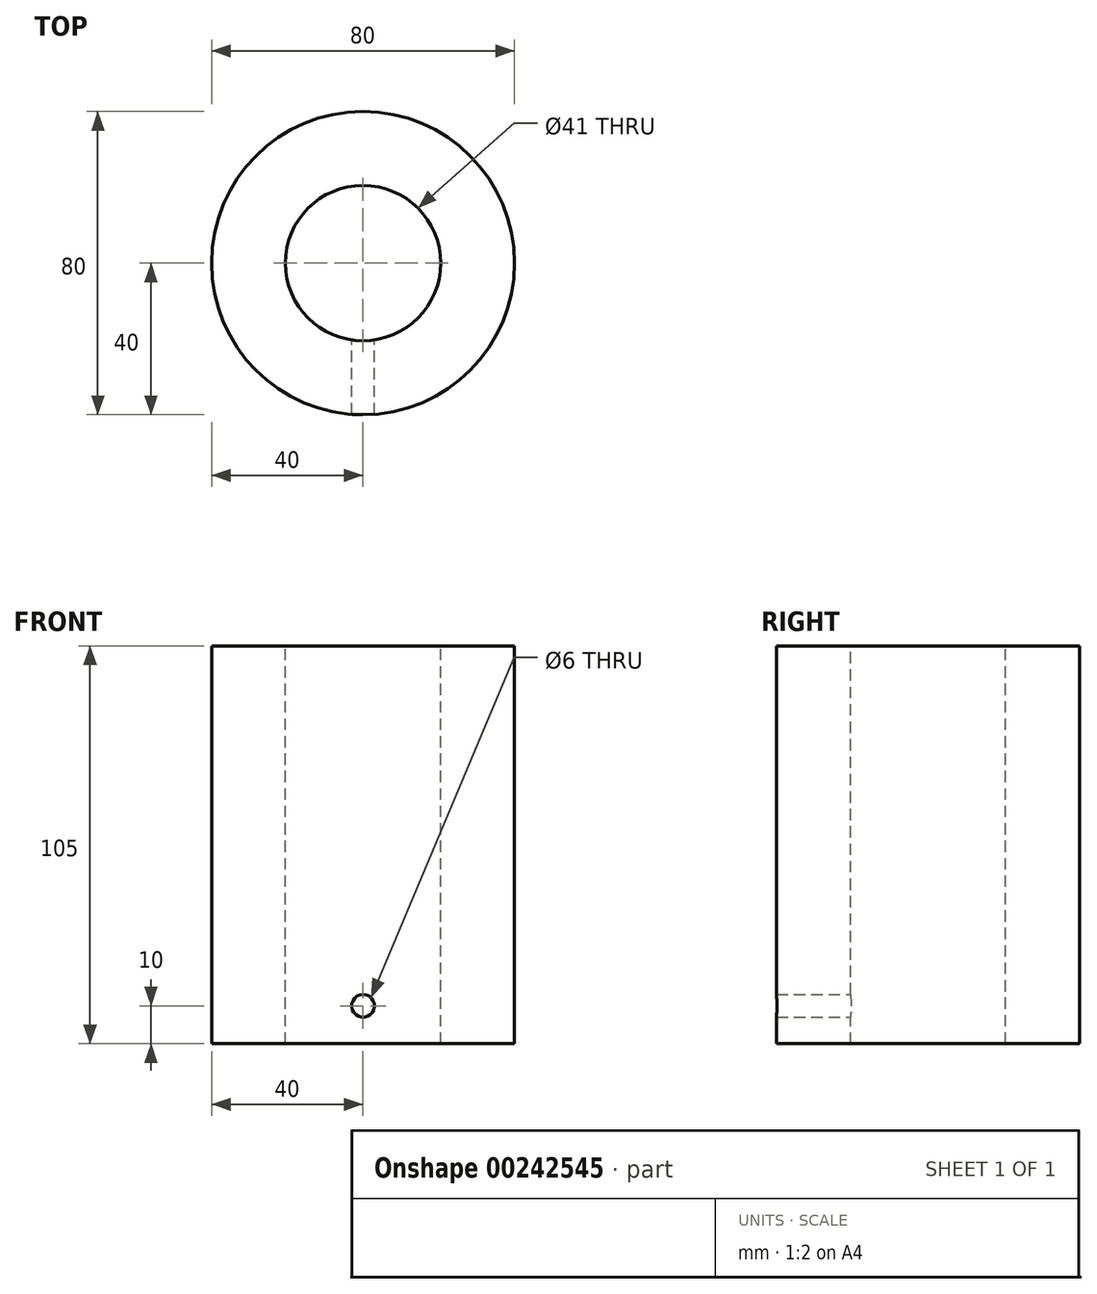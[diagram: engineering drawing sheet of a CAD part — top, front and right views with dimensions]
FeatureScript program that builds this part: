
annotation { "Feature Type Name" : "Feature", "Feature Type Description" : "" }
export const myFeature = defineFeature(function(context is Context, id is Id, definition is map)
    precondition{}
    {
        {
            var Q0;
            Q0=qCreatedBy(makeId("Top.planeOp"),FACE);
            var sketch = newSketch(context, id + "F0", { "sketchPlane" : qUnion([Q0])});
            skCircle(sketch, "E0", {"center": v(0, 0) * mm, "radius": 40 * mm});
            skSolve(sketch);
        }
        {
            var Q0;
            Q0=makeQuery(id+"F0.imprint","IMPRINT",FACE,{"disambiguationData":[TD([[makeQuery(id+"F0.imprint","IMPRINT",EDGE,{"derivedFrom":sQuery(id+"F0.wireOp",EDGE,"E0")}),1.0]])]});
            var Q1;
            Q1=sQuery(id+"F0.wireOp",EDGE,"E0");
            extrude(context, id + "F1", {"entities" : qUnion([Q0]), "surfaceEntities" : qUnion([Q1]), "depth" : 105 * mm});
        }
        {
            var Q0;
            Q0=makeQuery(id+"F1.opExtrude","CAP_FACE",FACE,{"disambiguationData":[OSD([sQuery(id+"F0.wireOp",EDGE,"E0")])],"isStart":false});
            var sketch = newSketch(context, id + "F2", { "sketchPlane" : qUnion([Q0])});
            skCircle(sketch, "E1", {"center": v(0, 0) * mm, "radius": 20.5 * mm});
            skSolve(sketch);
        }
        {
            var Q0;
            Q0 = qSketchRegion(id + "F2", true);
            extrude(context, id + "F3", {"entities" : qUnion([Q0]), "operationType" : NewBodyOperationType.REMOVE, "endBound" : BoundingType.THROUGH_ALL, "oppositeDirection" : true, "depth" : 25 * mm});
        }
        {
            var Q0;
            Q0=qCreatedBy(makeId("Front.planeOp"),FACE);
            var sketch = newSketch(context, id + "F4", { "sketchPlane" : qUnion([Q0])});
            skCircle(sketch, "E2", {"center": v(0, 10) * mm, "radius": 3 * mm});
            skSolve(sketch);
        }
        {
            var Q0;
            Q0 = qSketchRegion(id + "F4", true);
            extrude(context, id + "F5", {"entities" : qUnion([Q0]), "operationType" : NewBodyOperationType.REMOVE, "endBound" : BoundingType.THROUGH_ALL, "depth" : 25 * mm});
        }
    });
